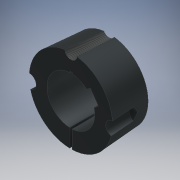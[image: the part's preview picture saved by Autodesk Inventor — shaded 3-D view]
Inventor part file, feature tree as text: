
AUTODESK INVENTOR PART (.ipt)
format: ipt  version: 2018 (Build 220112000, 112)  size: 208,896 bytes
history: native  units: mm
features: sketch x9, extrude x7, hole x2, other x2
ambient origin geometry x8: Origin, YZ Plane, XZ Plane, XY Plane, X Axis, Y Axis, Z Axis, Center Point
bodies: Solido1 (feature_tree)
feature tree (20):
  extrude  "Estrusione1"  Depth=30.0mm
  extrude  "Estrusione2"  Depth=80.0mm
  hole  "Foro1"  [1 undecoded]
  hole  "Foro2"  [1 undecoded]
  extrude  "Estrusione3"  Depth=34.0mm TaperAngle=0.0deg
  extrude  "Estrusione4"  Depth=69.77mm
  extrude  "Estrusione5"  Depth=16.580628mm
  other  "Sformo faccia1"
  extrude  "Estrusione6"  Depth=16.580628mm
  extrude  "Estrusione7"  Depth=69.77mm
  sketch  "Schizzo1"
  sketch  "Schizzo2"
  sketch  "Schizzo3"
  sketch  "Schizzo4"
  sketch  "Schizzo5"
  sketch  "Schizzo6"
  other  "Linea chiusa proiettata1"
  sketch  "Schizzo7"
  sketch  "Schizzo8"
  sketch  "Schizzo9"
note: 2 required parameter values undecoded (feature->parameter linkage not recoverable at this tier; creation-order binding heuristic only, values carry confidence <= 0.55)
